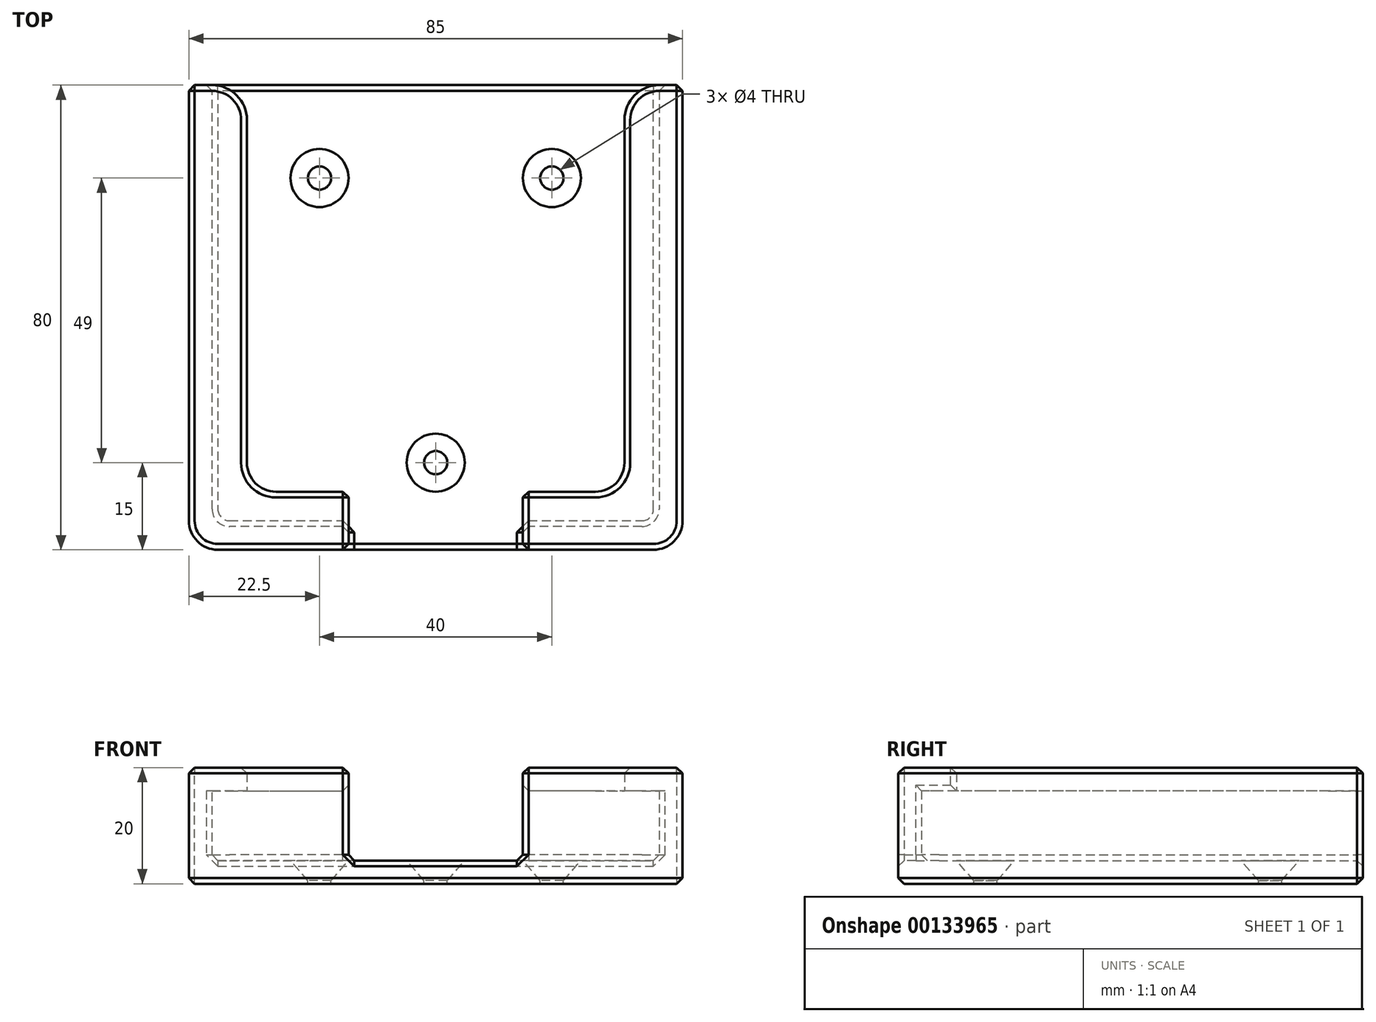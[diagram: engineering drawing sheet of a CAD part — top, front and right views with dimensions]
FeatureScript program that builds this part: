
annotation { "Feature Type Name" : "Feature", "Feature Type Description" : "" }
export const myFeature = defineFeature(function(context is Context, id is Id, definition is map)
    precondition{}
    {
        {
            var Q0;
            Q0=qCreatedBy(makeId("Top.planeOp"),FACE);
            var sketch = newSketch(context, id + "F0", { "sketchPlane" : qUnion([Q0])});
            skLineSegment(sketch, "E0.bottom", {"start": v(42.5, -40) * mm, "end": v(-42.5, -40) * mm});
            skLineSegment(sketch, "E0.top", {"start": v(42.5, 40) * mm, "end": v(-42.5, 40) * mm});
            skLineSegment(sketch, "E0.left", {"start": v(42.5, -40) * mm, "end": v(42.5, 40) * mm});
            skLineSegment(sketch, "E0.right", {"start": v(-42.5, -40) * mm, "end": v(-42.5, 40) * mm});
            skPoint(sketch, "E0.middle", {"position": v(0, 0) * mm});
            skSolve(sketch);
        }
        {
            var Q0;
            Q0=makeQuery(id+"F0.imprint","IMPRINT",FACE,{"disambiguationData":[TD([[makeQuery(id+"F0.imprint","IMPRINT",EDGE,{"derivedFrom":sQuery(id+"F0.wireOp",EDGE,"E0.bottom")}),-1.0]])]});
            extrude(context, id + "F1", {"entities" : qUnion([Q0]), "depth" : 4 * mm, "offsetDistance" : 25 * mm});
        }
        {
            var Q0;
            Q0=makeQuery(id+"F1.opExtrude","CAP_FACE",FACE,{"disambiguationData":[OSD([sQuery(id+"F0.wireOp",EDGE,"E0.bottom"),sQuery(id+"F0.wireOp",EDGE,"E0.top"),sQuery(id+"F0.wireOp",EDGE,"E0.left"),sQuery(id+"F0.wireOp",EDGE,"E0.right")])],"isStart":false});
            var sketch = newSketch(context, id + "F2", { "sketchPlane" : qUnion([Q0])});
            skLineSegment(sketch, "E1.0", {"start": v(-42.5, -40) * mm, "end": v(-42.5, 40) * mm});
            skLineSegment(sketch, "E2.0", {"start": v(-15, -40) * mm, "end": v(-42.5, -40) * mm});
            skLineSegment(sketch, "E3", {"start": v(-38.5, 40) * mm, "end": v(-38.5, -36) * mm});
            skLineSegment(sketch, "E4", {"start": v(-38.5, -36) * mm, "end": v(-15, -36) * mm});
            skLineSegment(sketch, "E5", {"start": v(0, 48.93) * mm, "end": v(0, -52.62) * mm, "construction": true});
            skLineSegment(sketch, "E6.trimOffspring", {"start": v(-38.5, 40) * mm, "end": v(-42.5, 40) * mm});
            skLineSegment(sketch, "E7", {"start": v(-15, -36) * mm, "end": v(-15, -40) * mm});
            skLineSegment(sketch, "E8.MirrorCS", {"start": v(38.5, 40) * mm, "end": v(38.5, -36) * mm});
            skLineSegment(sketch, "E9.MirrorCS", {"start": v(38.5, 40) * mm, "end": v(42.5, 40) * mm});
            skLineSegment(sketch, "E10.MirrorCS", {"start": v(42.5, -40) * mm, "end": v(42.5, 40) * mm});
            skLineSegment(sketch, "E11.MirrorCS", {"start": v(15, -36) * mm, "end": v(15, -40) * mm});
            skLineSegment(sketch, "E12.MirrorCS", {"start": v(15, -40) * mm, "end": v(42.5, -40) * mm});
            skLineSegment(sketch, "E13.MirrorCS", {"start": v(38.5, -36) * mm, "end": v(15, -36) * mm});
            skSolve(sketch);
        }
        {
            var Q0;
            Q0 = qSketchRegion(id + "F2", true);
            extrude(context, id + "F3", {"entities" : qUnion([Q0]), "operationType" : NewBodyOperationType.ADD, "depth" : 12 * mm, "offsetDistance" : 25 * mm});
        }
        {
            var Q0;
            Q0=makeQuery(id+"F3.opExtrude","CAP_FACE",FACE,{"disambiguationData":[OSD([sQuery(id+"F2.wireOp",EDGE,"E1.0"),sQuery(id+"F2.wireOp",EDGE,"E2.0"),sQuery(id+"F2.wireOp",EDGE,"E3"),sQuery(id+"F2.wireOp",EDGE,"E4"),sQuery(id+"F2.wireOp",EDGE,"E6.trimOffspring"),sQuery(id+"F2.wireOp",EDGE,"E7")])],"isStart":false});
            var sketch = newSketch(context, id + "F4", { "sketchPlane" : qUnion([Q0])});
            skLineSegment(sketch, "E14.0", {"start": v(-42.5, -40) * mm, "end": v(-42.5, 40) * mm});
            skLineSegment(sketch, "E15.0", {"start": v(-38.5, 40) * mm, "end": v(-42.5, 40) * mm});
            skLineSegment(sketch, "E16.0", {"start": v(-15, -40) * mm, "end": v(-42.5, -40) * mm});
            skLineSegment(sketch, "E17.0", {"start": v(-15, -36) * mm, "end": v(-15, -40) * mm});
            skLineSegment(sketch, "E18", {"start": v(0, 44.5) * mm, "end": v(0, -52.07) * mm, "construction": true});
            skLineSegment(sketch, "E19", {"start": v(-32.5, 40) * mm, "end": v(-32.5, -25) * mm});
            skPoint(sketch, "E19.startSnap0", {"position": v(-40.5, 40) * mm});
            skLineSegment(sketch, "E20", {"start": v(-27.5, -30) * mm, "end": v(-15, -30) * mm});
            skLineSegment(sketch, "E21", {"start": v(-15, -30) * mm, "end": v(-15, -36) * mm});
            skLineSegment(sketch, "E22", {"start": v(-32.5, 40) * mm, "end": v(-38.5, 40) * mm});
            skPoint(sketch, "E23.visualSharp", {"position": v(-32.5, -30) * mm});
            skArc(sketch, "E23.filletArc", {"start": v(-32.5, -25) * mm, "mid": v(-31.04, -28.54) * mm, "end": v(-27.5, -30) * mm});
            skLineSegment(sketch, "E24.MirrorCS", {"start": v(32.5, 40) * mm, "end": v(32.5, -25) * mm});
            skArc(sketch, "E25.MirrorCS", {"start": v(32.5, -25) * mm, "mid": v(31.04, -28.54) * mm, "end": v(27.5, -30) * mm});
            skLineSegment(sketch, "E26.MirrorCS", {"start": v(27.5, -30) * mm, "end": v(15, -30) * mm});
            skLineSegment(sketch, "E27.MirrorCS", {"start": v(15, -30) * mm, "end": v(15, -36) * mm});
            skLineSegment(sketch, "E28.MirrorCS", {"start": v(15, -36) * mm, "end": v(15, -40) * mm});
            skLineSegment(sketch, "E29.MirrorCS", {"start": v(15, -40) * mm, "end": v(42.5, -40) * mm});
            skLineSegment(sketch, "E30.MirrorCS", {"start": v(42.5, -40) * mm, "end": v(42.5, 40) * mm});
            skLineSegment(sketch, "E31.MirrorCS", {"start": v(38.5, 40) * mm, "end": v(42.5, 40) * mm});
            skLineSegment(sketch, "E32.MirrorCS", {"start": v(32.5, 40) * mm, "end": v(38.5, 40) * mm});
            skSolve(sketch);
        }
        {
            var Q0;
            Q0 = qSketchRegion(id + "F4", true);
            extrude(context, id + "F5", {"entities" : qUnion([Q0]), "operationType" : NewBodyOperationType.ADD, "depth" : 4 * mm, "offsetDistance" : 25 * mm});
        }
        {
            var Q0;
            Q0=makeQuery(id+"F5.boolean.opBoolean","MERGE",EDGE,{"derivedFrom":[makeQuery(id+"F3.boolean.opBoolean","MERGE",EDGE,{"derivedFrom":[makeQuery(id+"F1.opExtrude","SWEPT_EDGE",EDGE,{"disambiguationData":[OSD([sQuery(id+"F0.wireOp",EDGE,"E0.bottom"),sQuery(id+"F0.wireOp",EDGE,"E0.right")])]}),makeQuery(id+"F3.opExtrude","SWEPT_EDGE",EDGE,{"disambiguationData":[OSD([sQuery(id+"F2.wireOp",EDGE,"E1.0"),sQuery(id+"F2.wireOp",EDGE,"E2.0")])]})]}),makeQuery(id+"F5.opExtrude","SWEPT_EDGE",EDGE,{"disambiguationData":[OSD([sQuery(id+"F4.wireOp",EDGE,"E14.0"),sQuery(id+"F4.wireOp",EDGE,"E16.0")])]})]});
            var Q1;
            Q1=makeQuery(id+"F5.boolean.opBoolean","MERGE",EDGE,{"derivedFrom":[makeQuery(id+"F3.boolean.opBoolean","MERGE",EDGE,{"derivedFrom":[makeQuery(id+"F1.opExtrude","SWEPT_EDGE",EDGE,{"disambiguationData":[OSD([sQuery(id+"F0.wireOp",EDGE,"E0.bottom"),sQuery(id+"F0.wireOp",EDGE,"E0.left")])]}),makeQuery(id+"F3.opExtrude","SWEPT_EDGE",EDGE,{"disambiguationData":[OSD([sQuery(id+"F2.wireOp",EDGE,"E10.MirrorCS"),sQuery(id+"F2.wireOp",EDGE,"E12.MirrorCS")])]})]}),makeQuery(id+"F5.opExtrude","SWEPT_EDGE",EDGE,{"disambiguationData":[OSD([sQuery(id+"F4.wireOp",EDGE,"E29.MirrorCS"),sQuery(id+"F4.wireOp",EDGE,"E30.MirrorCS")])]})]});
            fillet(context, id + "F6", {"entities" : qUnion([Q0, Q1]), "radius" : 5 * mm, "tangentPropagation" : true, "allowEdgeOverflow" : false});
        }
        {
            var Q0;
            Q0=makeQuery(id+"F3.opExtrude","SWEPT_EDGE",EDGE,{"disambiguationData":[OSD([sQuery(id+"F2.wireOp",EDGE,"E8.MirrorCS"),sQuery(id+"F2.wireOp",EDGE,"E13.MirrorCS")])]});
            var Q1;
            Q1=makeQuery(id+"F3.opExtrude","SWEPT_EDGE",EDGE,{"disambiguationData":[OSD([sQuery(id+"F2.wireOp",EDGE,"E3"),sQuery(id+"F2.wireOp",EDGE,"E4")])]});
            fillet(context, id + "F7", {"entities" : qUnion([Q0, Q1]), "radius" : 3 * mm, "tangentPropagation" : true, "allowEdgeOverflow" : false});
        }
        {
            var Q0;
            Q0=makeQuery(id+"F5.opExtrude","SWEPT_EDGE",EDGE,{"disambiguationData":[OSD([sQuery(id+"F4.wireOp",EDGE,"E19"),sQuery(id+"F4.wireOp",EDGE,"E22")])]});
            var Q1;
            Q1=makeQuery(id+"F5.opExtrude","SWEPT_EDGE",EDGE,{"disambiguationData":[OSD([sQuery(id+"F4.wireOp",EDGE,"E24.MirrorCS"),sQuery(id+"F4.wireOp",EDGE,"E32.MirrorCS")])]});
            fillet(context, id + "F8", {"entities" : qUnion([Q0, Q1]), "radius" : 6 * mm, "tangentPropagation" : true, "allowEdgeOverflow" : false});
        }
        {
            var Q0;
            Q0=makeQuery(id+"F5.boolean.opBoolean","MERGE",FACE,{"derivedFrom":[makeQuery(id+"F3.boolean.opBoolean","MERGE",FACE,{"derivedFrom":[makeQuery(id+"F1.opExtrude","SWEPT_FACE",FACE,{"disambiguationData":[OSD([sQuery(id+"F0.wireOp",EDGE,"E0.top")])]}),makeQuery(id+"F3.opExtrude","SWEPT_FACE",FACE,{"disambiguationData":[OSD([sQuery(id+"F2.wireOp",EDGE,"E6.trimOffspring")])]}),makeQuery(id+"F3.opExtrude","SWEPT_FACE",FACE,{"disambiguationData":[OSD([sQuery(id+"F2.wireOp",EDGE,"E9.MirrorCS")])]})]}),makeQuery(id+"F5.opExtrude","SWEPT_FACE",FACE,{"disambiguationData":[OSD([sQuery(id+"F4.wireOp",EDGE,"E15.0"),sQuery(id+"F4.wireOp",EDGE,"E22")])]}),makeQuery(id+"F5.opExtrude","SWEPT_FACE",FACE,{"disambiguationData":[OSD([sQuery(id+"F4.wireOp",EDGE,"E31.MirrorCS"),sQuery(id+"F4.wireOp",EDGE,"E32.MirrorCS")])]})]});
            var Q1;
            Q1=makeQuery(id+"F5.boolean.opBoolean","MERGE",FACE,{"derivedFrom":[makeQuery(id+"F3.boolean.opBoolean","MERGE",FACE,{"derivedFrom":[makeQuery(id+"F1.opExtrude","SWEPT_FACE",FACE,{"disambiguationData":[OSD([sQuery(id+"F0.wireOp",EDGE,"E0.bottom")])]}),makeQuery(id+"F3.opExtrude","SWEPT_FACE",FACE,{"disambiguationData":[OSD([sQuery(id+"F2.wireOp",EDGE,"E2.0")])]}),makeQuery(id+"F3.opExtrude","SWEPT_FACE",FACE,{"disambiguationData":[OSD([sQuery(id+"F2.wireOp",EDGE,"E12.MirrorCS")])]})]}),makeQuery(id+"F5.opExtrude","SWEPT_FACE",FACE,{"disambiguationData":[OSD([sQuery(id+"F4.wireOp",EDGE,"E16.0")])]}),makeQuery(id+"F5.opExtrude","SWEPT_FACE",FACE,{"disambiguationData":[OSD([sQuery(id+"F4.wireOp",EDGE,"E29.MirrorCS")])]})]});
            var Q2;
            Q2=makeQuery(id+"F6.opFillet","BLEND_FACE",FACE,{"disambiguationData":[OSD([sQuery(id+"F0.wireOp",EDGE,"E0.bottom"),sQuery(id+"F0.wireOp",EDGE,"E0.left"),sQuery(id+"F2.wireOp",EDGE,"E10.MirrorCS"),sQuery(id+"F2.wireOp",EDGE,"E12.MirrorCS"),sQuery(id+"F4.wireOp",EDGE,"E29.MirrorCS"),sQuery(id+"F4.wireOp",EDGE,"E30.MirrorCS")])]});
            var Q3;
            Q3=makeQuery(id+"F5.boolean.opBoolean","MERGE",FACE,{"derivedFrom":[makeQuery(id+"F3.boolean.opBoolean","MERGE",FACE,{"derivedFrom":[makeQuery(id+"F1.opExtrude","SWEPT_FACE",FACE,{"disambiguationData":[OSD([sQuery(id+"F0.wireOp",EDGE,"E0.left")])]}),makeQuery(id+"F3.opExtrude","SWEPT_FACE",FACE,{"disambiguationData":[OSD([sQuery(id+"F2.wireOp",EDGE,"E10.MirrorCS")])]})]}),makeQuery(id+"F5.opExtrude","SWEPT_FACE",FACE,{"disambiguationData":[OSD([sQuery(id+"F4.wireOp",EDGE,"E30.MirrorCS")])]})]});
            var Q4;
            Q4=makeQuery(id+"F6.opFillet","BLEND_FACE",FACE,{"disambiguationData":[OSD([sQuery(id+"F0.wireOp",EDGE,"E0.bottom"),sQuery(id+"F0.wireOp",EDGE,"E0.right"),sQuery(id+"F2.wireOp",EDGE,"E1.0"),sQuery(id+"F2.wireOp",EDGE,"E2.0"),sQuery(id+"F4.wireOp",EDGE,"E14.0"),sQuery(id+"F4.wireOp",EDGE,"E16.0")])]});
            var Q5;
            Q5=makeQuery(id+"F5.boolean.opBoolean","MERGE",FACE,{"derivedFrom":[makeQuery(id+"F3.boolean.opBoolean","MERGE",FACE,{"derivedFrom":[makeQuery(id+"F1.opExtrude","SWEPT_FACE",FACE,{"disambiguationData":[OSD([sQuery(id+"F0.wireOp",EDGE,"E0.right")])]}),makeQuery(id+"F3.opExtrude","SWEPT_FACE",FACE,{"disambiguationData":[OSD([sQuery(id+"F2.wireOp",EDGE,"E1.0")])]})]}),makeQuery(id+"F5.opExtrude","SWEPT_FACE",FACE,{"disambiguationData":[OSD([sQuery(id+"F4.wireOp",EDGE,"E14.0")])]})]});
            var Q6;
            Q6=makeQuery(id+"F1.opExtrude","CAP_FACE",FACE,{"disambiguationData":[OSD([sQuery(id+"F0.wireOp",EDGE,"E0.bottom"),sQuery(id+"F0.wireOp",EDGE,"E0.top"),sQuery(id+"F0.wireOp",EDGE,"E0.left"),sQuery(id+"F0.wireOp",EDGE,"E0.right")])],"isStart":true});
            var Q7;
            Q7=makeQuery(id+"F1.opExtrude","CAP_FACE",FACE,{"disambiguationData":[OSD([sQuery(id+"F0.wireOp",EDGE,"E0.bottom"),sQuery(id+"F0.wireOp",EDGE,"E0.top"),sQuery(id+"F0.wireOp",EDGE,"E0.left"),sQuery(id+"F0.wireOp",EDGE,"E0.right")])],"isStart":false});
            var Q8;
            Q8=makeQuery(id+"F5.boolean.opBoolean","MERGE",FACE,{"derivedFrom":[makeQuery(id+"F3.opExtrude","SWEPT_FACE",FACE,{"disambiguationData":[OSD([sQuery(id+"F2.wireOp",EDGE,"E11.MirrorCS")])]}),makeQuery(id+"F5.opExtrude","SWEPT_FACE",FACE,{"disambiguationData":[OSD([sQuery(id+"F4.wireOp",EDGE,"E27.MirrorCS"),sQuery(id+"F4.wireOp",EDGE,"E28.MirrorCS")])]})]});
            var Q9;
            Q9=makeQuery(id+"F5.boolean.opBoolean","MERGE",FACE,{"derivedFrom":[makeQuery(id+"F3.opExtrude","SWEPT_FACE",FACE,{"disambiguationData":[OSD([sQuery(id+"F2.wireOp",EDGE,"E7")])]}),makeQuery(id+"F5.opExtrude","SWEPT_FACE",FACE,{"disambiguationData":[OSD([sQuery(id+"F4.wireOp",EDGE,"E17.0"),sQuery(id+"F4.wireOp",EDGE,"E21")])]})]});
            chamfer(context, id + "F9", {"entities" : qUnion([Q0, Q1, Q2, Q3, Q4, Q5, Q6, Q7, Q8, Q9]), "width" : 1 * mm, "tangentPropagation" : true});
        }
        {
            var Q0;
            Q0=makeQuery(id+"F1.opExtrude","CAP_FACE",FACE,{"disambiguationData":[OSD([sQuery(id+"F0.wireOp",EDGE,"E0.bottom"),sQuery(id+"F0.wireOp",EDGE,"E0.top"),sQuery(id+"F0.wireOp",EDGE,"E0.left"),sQuery(id+"F0.wireOp",EDGE,"E0.right")])],"isStart":false});
            var sketch = newSketch(context, id + "F10", { "sketchPlane" : qUnion([Q0])});
            skPoint(sketch, "E33", {"position": v(-20, 24) * mm});
            skPoint(sketch, "E34", {"position": v(20, 24) * mm});
            skPoint(sketch, "E35", {"position": v(0, -25) * mm});
            skSolve(sketch);
        }
        {
            var Q0;
            Q0=sQuery(id+"F10.wireOp",VERTEX,"E33");
            var Q1;
            Q1=sQuery(id+"F10.wireOp",VERTEX,"E34");
            var Q2;
            Q2=sQuery(id+"F10.wireOp",VERTEX,"E35");
            var Q3;
            Q3=makeQuery(id+"F1.opExtrude","SWEPT_BODY",BODY,{"disambiguationData":[OSD([sQuery(id+"F0.wireOp",EDGE,"E0.bottom"),sQuery(id+"F0.wireOp",EDGE,"E0.top"),sQuery(id+"F0.wireOp",EDGE,"E0.left"),sQuery(id+"F0.wireOp",EDGE,"E0.right")])]});
            hole(context, id + "F11", {"style" : HoleStyle.C_SINK, "endStyle" : HoleEndStyle.THROUGH, "holeDiameter" : 4 * mm, "cSinkDiameter" : 10 * mm, "cSinkAngle" : 82 * degree, "majorDiameter" : 5 * mm, "isTappedThrough" : true, "tappedDepth" : 12 * mm, "tapClearance" : 3, "startFromSketch" : true, "locations" : qUnion([Q0, Q1, Q2]), "scope" : qUnion([Q3])});
        }
    });
